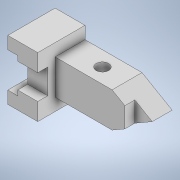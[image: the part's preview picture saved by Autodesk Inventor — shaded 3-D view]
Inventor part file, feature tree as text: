
AUTODESK INVENTOR PART (.ipt)
format: ipt  version: 2022 (Build 260153000, 153)  size: 143,872 bytes
history: native  units: mm
features: extrude x5, sketch x2, other x1
ambient origin geometry x8: Origin, YZ Plane, XZ Plane, XY Plane, X Axis, Y Axis, Z Axis, Center Point
bodies: Body1 (feature_tree)
feature tree (8):
  other  "Sólido1"
  sketch  "Esboço1"  dims[d13=24.0mm d14=60.0deg]
  extrude  "Extrusão1"  TaperAngle=60.0deg  [1 undecoded]
  extrude  "Extrusão2"  Depth=26.0mm
  extrude  "Extrusão3"  Depth=8.0mm
  extrude  "Extrusão4"  Depth=16.0mm
  extrude  "Extrusão5"  Depth=48.0mm
  sketch  "Esboço2"  dims[d15=28.0mm d16=94.0mm d17=8.0mm d18=16.0mm d19=48.0mm d20=28.0mm d21=20.0mm d22=90.0deg d23=14.0mm d24=38.0mm d25=0.0mm d26=30.0mm d27=0.0mm d28=24.0mm d29=0.0mm d30=16.0mm d31=0.0mm d32=10.0mm d33=12.0mm d34=26.0mm d35=0.0mm d36=0.0mm]
note: 1 required parameter value undecoded (feature->parameter linkage not recoverable at this tier; creation-order binding heuristic only, values carry confidence <= 0.55)
